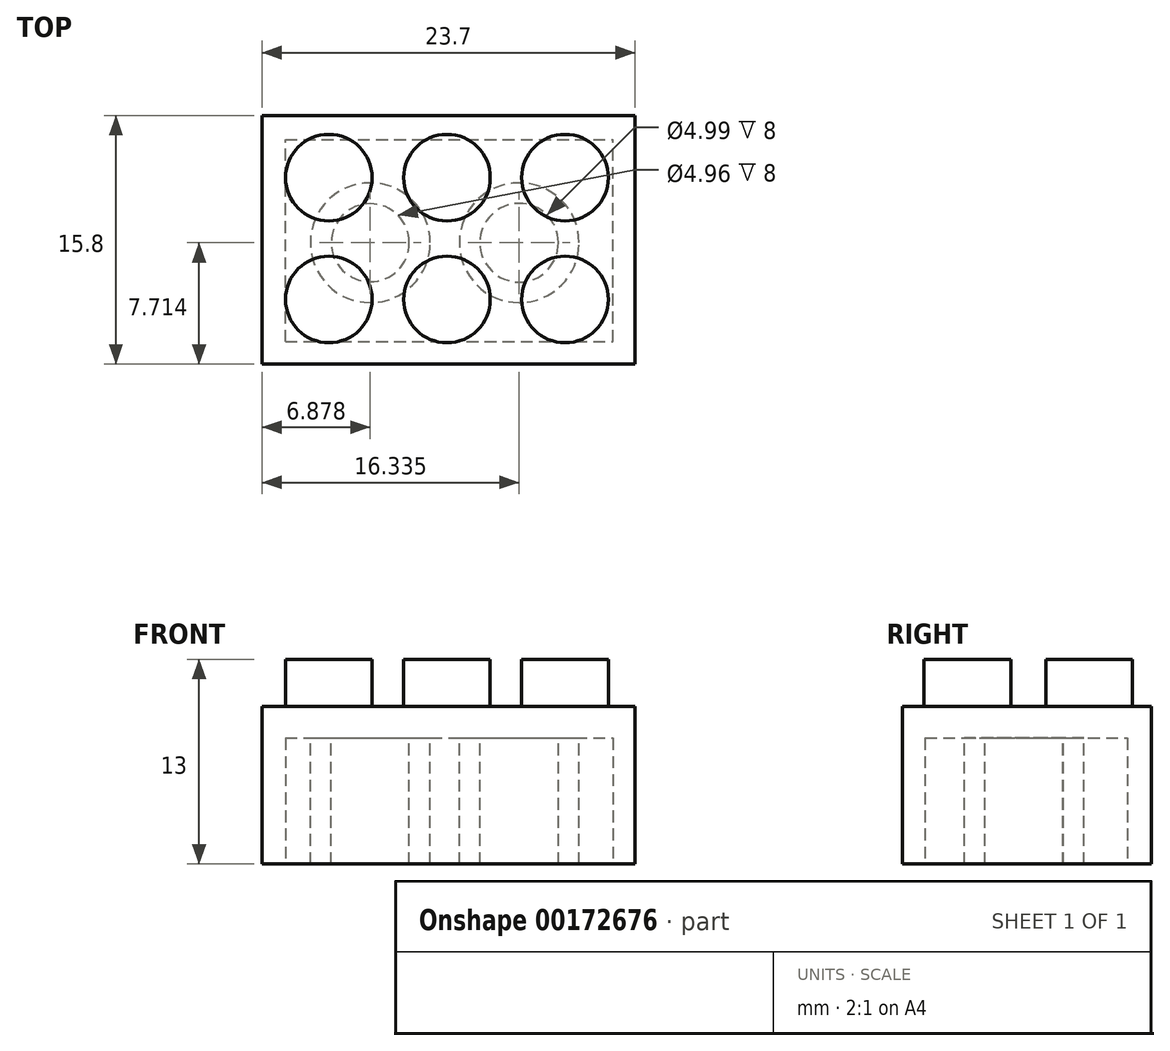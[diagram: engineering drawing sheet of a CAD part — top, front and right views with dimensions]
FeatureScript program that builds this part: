
annotation { "Feature Type Name" : "Feature", "Feature Type Description" : "" }
export const myFeature = defineFeature(function(context is Context, id is Id, definition is map)
    precondition{}
    {
        {
            var Q0;
            Q0=qCreatedBy(makeId("Top.planeOp"),FACE);
            var sketch = newSketch(context, id + "F0", { "sketchPlane" : qUnion([Q0])});
            skLineSegment(sketch, "E0.bottom", {"start": v(0, 0) * mm, "end": v(23.7, 0) * mm});
            skLineSegment(sketch, "E0.top", {"start": v(0, 15.8) * mm, "end": v(23.7, 15.8) * mm});
            skLineSegment(sketch, "E0.left", {"start": v(0, 0) * mm, "end": v(0, 15.8) * mm});
            skLineSegment(sketch, "E0.right", {"start": v(23.7, 0) * mm, "end": v(23.7, 15.8) * mm});
            skSolve(sketch);
        }
        {
            var Q0;
            Q0 = qSketchRegion(id + "F0", true);
            extrude(context, id + "F1", {"entities" : qUnion([Q0]), "depth" : 10 * mm});
        }
        {
            var Q0;
            Q0=makeQuery(id+"F1.opExtrude","CAP_FACE",FACE,{"disambiguationData":[OSD([sQuery(id+"F0.wireOp",EDGE,"E0.bottom"),sQuery(id+"F0.wireOp",EDGE,"E0.top"),sQuery(id+"F0.wireOp",EDGE,"E0.left"),sQuery(id+"F0.wireOp",EDGE,"E0.right")])],"isStart":false});
            var sketch = newSketch(context, id + "F2", { "sketchPlane" : qUnion([Q0])});
            skCircle(sketch, "E1", {"center": v(4.25, 11.85) * mm, "radius": 2.75 * mm});
            skCircle(sketch, "E2.1.0.0", {"center": v(11.75, 11.85) * mm, "radius": 2.75 * mm});
            skCircle(sketch, "E2.2.0.0", {"center": v(19.25, 11.85) * mm, "radius": 2.75 * mm});
            skLineSegment(sketch, "E2.direction1", {"start": v(4.25, 11.85) * mm, "end": v(11.75, 11.85) * mm, "construction": true});
            skCircle(sketch, "E3", {"center": v(4.25, 4.12) * mm, "radius": 2.75 * mm});
            skCircle(sketch, "E4.1.0.0", {"center": v(11.75, 4.12) * mm, "radius": 2.75 * mm});
            skCircle(sketch, "E4.2.0.0", {"center": v(19.25, 4.12) * mm, "radius": 2.75 * mm});
            skLineSegment(sketch, "E4.direction1", {"start": v(4.25, 4.12) * mm, "end": v(11.75, 4.12) * mm, "construction": true});
            skSolve(sketch);
        }
        {
            var Q0;
            Q0 = qSketchRegion(id + "F2", true);
            extrude(context, id + "F3", {"entities" : qUnion([Q0]), "operationType" : NewBodyOperationType.ADD, "depth" : 3 * mm});
        }
        {
            var Q0;
            Q0=makeQuery(id+"F1.opExtrude","CAP_FACE",FACE,{"disambiguationData":[OSD([sQuery(id+"F0.wireOp",EDGE,"E0.bottom"),sQuery(id+"F0.wireOp",EDGE,"E0.top"),sQuery(id+"F0.wireOp",EDGE,"E0.left"),sQuery(id+"F0.wireOp",EDGE,"E0.right")])],"isStart":true});
            var sketch = newSketch(context, id + "F4", { "sketchPlane" : qUnion([Q0])});
            skLineSegment(sketch, "E5.bottom", {"start": v(1.5, -1.43) * mm, "end": v(22.28, -1.43) * mm});
            skLineSegment(sketch, "E5.top", {"start": v(1.5, -14.27) * mm, "end": v(22.28, -14.27) * mm});
            skLineSegment(sketch, "E5.left", {"start": v(1.5, -1.43) * mm, "end": v(1.5, -14.27) * mm});
            skLineSegment(sketch, "E5.right", {"start": v(22.28, -1.43) * mm, "end": v(22.28, -14.27) * mm});
            skSolve(sketch);
        }
        {
            var Q0;
            Q0 = qSketchRegion(id + "F4", true);
            extrude(context, id + "F5", {"entities" : qUnion([Q0]), "operationType" : NewBodyOperationType.REMOVE, "oppositeDirection" : true, "depth" : 8 * mm});
        }
        {
            var Q0;
            Q0=makeQuery(id+"F5.boolean.opBoolean","COPY",FACE,{"derivedFrom":makeQuery(id+"F5.opExtrude","CAP_FACE",FACE,{"disambiguationData":[OSD([sQuery(id+"F4.wireOp",EDGE,"E5.bottom"),sQuery(id+"F4.wireOp",EDGE,"E5.top"),sQuery(id+"F4.wireOp",EDGE,"E5.left"),sQuery(id+"F4.wireOp",EDGE,"E5.right")])],"isStart":false})});
            var sketch = newSketch(context, id + "F6", { "sketchPlane" : qUnion([Q0])});
            skCircle(sketch, "E6", {"center": v(16.34, -7.71) * mm, "radius": 3.8 * mm});
            skCircle(sketch, "E7", {"center": v(6.88, -7.71) * mm, "radius": 3.8 * mm});
            skCircle(sketch, "E8", {"center": v(6.88, -7.71) * mm, "radius": 2.48 * mm});
            skCircle(sketch, "E9", {"center": v(16.34, -7.71) * mm, "radius": 2.5 * mm});
            skSolve(sketch);
        }
        {
            var Q0;
            Q0 = qSketchRegion(id + "F6", true);
            extrude(context, id + "F7", {"entities" : qUnion([Q0]), "operationType" : NewBodyOperationType.ADD, "depth" : 8 * mm});
        }
    });
